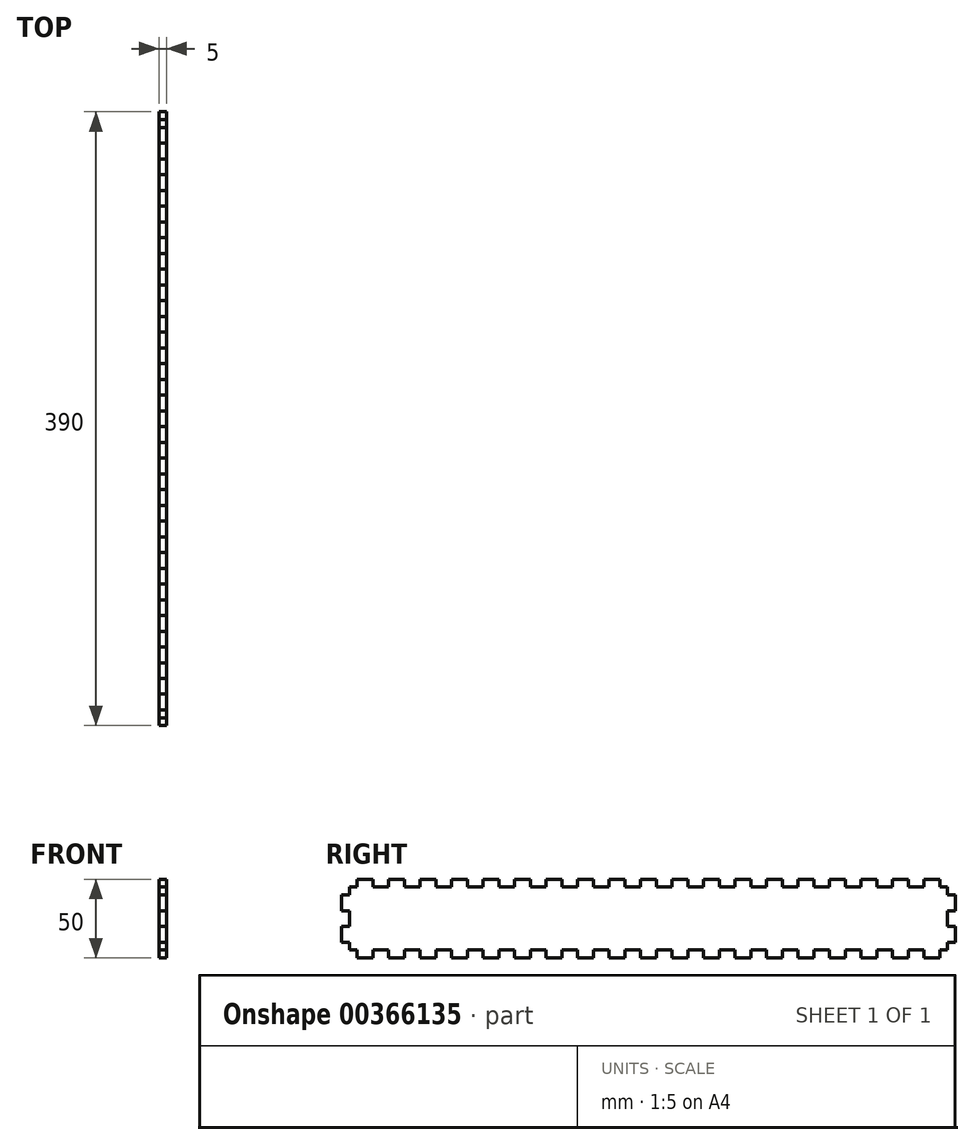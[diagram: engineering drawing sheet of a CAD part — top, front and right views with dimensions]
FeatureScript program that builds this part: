
annotation { "Feature Type Name" : "Feature", "Feature Type Description" : "" }
export const myFeature = defineFeature(function(context is Context, id is Id, definition is map)
    precondition{}
    {
        {
            var Q0;
            Q0=qCreatedBy(makeId("Right.planeOp"),FACE);
            var sketch = newSketch(context, id + "F0", { "sketchPlane" : qUnion([Q0])});
            skPoint(sketch, "E0.middle", {"position": v(0, 0) * mm});
            skLineSegment(sketch, "E1", {"start": v(-125, 20) * mm, "end": v(-125, 25) * mm});
            skLineSegment(sketch, "E2.1.0.0", {"start": v(-125, 25) * mm, "end": v(-115, 25) * mm});
            skLineSegment(sketch, "E2.1.0.1", {"start": v(-115, 25) * mm, "end": v(-115, 20) * mm});
            skLineSegment(sketch, "E2.1.0.2", {"start": v(-115, 20) * mm, "end": v(-105, 20) * mm});
            skLineSegment(sketch, "E2.1.0.3", {"start": v(-105, 20) * mm, "end": v(-105, 25) * mm});
            skLineSegment(sketch, "E2.2.0.0", {"start": v(-105, 25) * mm, "end": v(-95, 25) * mm});
            skLineSegment(sketch, "E2.2.0.1", {"start": v(-95, 25) * mm, "end": v(-95, 20) * mm});
            skLineSegment(sketch, "E2.2.0.2", {"start": v(-95, 20) * mm, "end": v(-85, 20) * mm});
            skLineSegment(sketch, "E2.2.0.3", {"start": v(-85, 20) * mm, "end": v(-85, 25) * mm});
            skLineSegment(sketch, "E2.3.0.0", {"start": v(-85, 25) * mm, "end": v(-75, 25) * mm});
            skLineSegment(sketch, "E2.3.0.1", {"start": v(-75, 25) * mm, "end": v(-75, 20) * mm});
            skLineSegment(sketch, "E2.3.0.2", {"start": v(-75, 20) * mm, "end": v(-65, 20) * mm});
            skLineSegment(sketch, "E2.3.0.3", {"start": v(-65, 20) * mm, "end": v(-65, 25) * mm});
            skLineSegment(sketch, "E2.4.0.0", {"start": v(-65, 25) * mm, "end": v(-55, 25) * mm});
            skLineSegment(sketch, "E2.4.0.1", {"start": v(-55, 25) * mm, "end": v(-55, 20) * mm});
            skLineSegment(sketch, "E2.4.0.2", {"start": v(-55, 20) * mm, "end": v(-45, 20) * mm});
            skLineSegment(sketch, "E2.4.0.3", {"start": v(-45, 20) * mm, "end": v(-45, 25) * mm});
            skLineSegment(sketch, "E2.5.0.0", {"start": v(-45, 25) * mm, "end": v(-35, 25) * mm});
            skLineSegment(sketch, "E2.5.0.1", {"start": v(-35, 25) * mm, "end": v(-35, 20) * mm});
            skLineSegment(sketch, "E2.5.0.2", {"start": v(-35, 20) * mm, "end": v(-25, 20) * mm});
            skLineSegment(sketch, "E2.5.0.3", {"start": v(-25, 20) * mm, "end": v(-25, 25) * mm});
            skLineSegment(sketch, "E2.6.0.0", {"start": v(-25, 25) * mm, "end": v(-15, 25) * mm});
            skLineSegment(sketch, "E2.6.0.1", {"start": v(-15, 25) * mm, "end": v(-15, 20) * mm});
            skLineSegment(sketch, "E2.6.0.2", {"start": v(-15, 20) * mm, "end": v(-5, 20) * mm});
            skLineSegment(sketch, "E2.6.0.3", {"start": v(-5, 20) * mm, "end": v(-5, 25) * mm});
            skLineSegment(sketch, "E2.7.0.0", {"start": v(-5, 25) * mm, "end": v(5, 25) * mm});
            skLineSegment(sketch, "E2.7.0.1", {"start": v(5, 25) * mm, "end": v(5, 20) * mm});
            skLineSegment(sketch, "E2.7.0.2", {"start": v(5, 20) * mm, "end": v(15, 20) * mm});
            skLineSegment(sketch, "E2.7.0.3", {"start": v(15, 20) * mm, "end": v(15, 25) * mm});
            skLineSegment(sketch, "E2.8.0.0", {"start": v(15, 25) * mm, "end": v(25, 25) * mm});
            skLineSegment(sketch, "E2.8.0.1", {"start": v(25, 25) * mm, "end": v(25, 20) * mm});
            skLineSegment(sketch, "E2.8.0.2", {"start": v(25, 20) * mm, "end": v(35, 20) * mm});
            skLineSegment(sketch, "E2.8.0.3", {"start": v(35, 20) * mm, "end": v(35, 25) * mm});
            skLineSegment(sketch, "E2.9.0.0", {"start": v(35, 25) * mm, "end": v(45, 25) * mm});
            skLineSegment(sketch, "E2.9.0.1", {"start": v(45, 25) * mm, "end": v(45, 20) * mm});
            skLineSegment(sketch, "E2.9.0.2", {"start": v(45, 20) * mm, "end": v(55, 20) * mm});
            skLineSegment(sketch, "E2.9.0.3", {"start": v(55, 20) * mm, "end": v(55, 25) * mm});
            skLineSegment(sketch, "E2.10.0.0", {"start": v(55, 25) * mm, "end": v(65, 25) * mm});
            skLineSegment(sketch, "E2.10.0.1", {"start": v(65, 25) * mm, "end": v(65, 20) * mm});
            skLineSegment(sketch, "E2.10.0.2", {"start": v(65, 20) * mm, "end": v(75, 20) * mm});
            skLineSegment(sketch, "E2.10.0.3", {"start": v(75, 20) * mm, "end": v(75, 25) * mm});
            skLineSegment(sketch, "E2.11.0.0", {"start": v(75, 25) * mm, "end": v(85, 25) * mm});
            skLineSegment(sketch, "E2.11.0.1", {"start": v(85, 25) * mm, "end": v(85, 20) * mm});
            skLineSegment(sketch, "E2.11.0.2", {"start": v(85, 20) * mm, "end": v(95, 20) * mm});
            skLineSegment(sketch, "E2.11.0.3", {"start": v(95, 20) * mm, "end": v(95, 25) * mm});
            skLineSegment(sketch, "E2.12.0.0", {"start": v(95, 25) * mm, "end": v(105, 25) * mm});
            skLineSegment(sketch, "E2.12.0.1", {"start": v(105, 25) * mm, "end": v(105, 20) * mm});
            skLineSegment(sketch, "E2.12.0.2", {"start": v(105, 20) * mm, "end": v(115, 20) * mm});
            skLineSegment(sketch, "E2.12.0.3", {"start": v(115, 20) * mm, "end": v(115, 25) * mm});
            skLineSegment(sketch, "E2.13.0.0", {"start": v(115, 25) * mm, "end": v(125, 25) * mm});
            skLineSegment(sketch, "E2.13.0.1", {"start": v(125, 25) * mm, "end": v(125, 20) * mm});
            skLineSegment(sketch, "E2.13.0.2", {"start": v(125, 20) * mm, "end": v(135, 20) * mm});
            skLineSegment(sketch, "E2.13.0.3", {"start": v(135, 20) * mm, "end": v(135, 25) * mm});
            skLineSegment(sketch, "E3", {"start": v(135, 25) * mm, "end": v(145, 25) * mm});
            skLineSegment(sketch, "E4", {"start": v(-125, -20) * mm, "end": v(-125, -25) * mm});
            skLineSegment(sketch, "E5.1.0.0", {"start": v(-125, -25) * mm, "end": v(-115, -25) * mm});
            skLineSegment(sketch, "E5.1.0.1", {"start": v(-115, -25) * mm, "end": v(-115, -20) * mm});
            skLineSegment(sketch, "E5.1.0.2", {"start": v(-115, -20) * mm, "end": v(-105, -20) * mm});
            skLineSegment(sketch, "E5.1.0.3", {"start": v(-105, -20) * mm, "end": v(-105, -25) * mm});
            skLineSegment(sketch, "E5.2.0.0", {"start": v(-105, -25) * mm, "end": v(-95, -25) * mm});
            skLineSegment(sketch, "E5.2.0.1", {"start": v(-95, -25) * mm, "end": v(-95, -20) * mm});
            skLineSegment(sketch, "E5.2.0.2", {"start": v(-95, -20) * mm, "end": v(-85, -20) * mm});
            skLineSegment(sketch, "E5.2.0.3", {"start": v(-85, -20) * mm, "end": v(-85, -25) * mm});
            skLineSegment(sketch, "E5.3.0.0", {"start": v(-85, -25) * mm, "end": v(-75, -25) * mm});
            skLineSegment(sketch, "E5.3.0.1", {"start": v(-75, -25) * mm, "end": v(-75, -20) * mm});
            skLineSegment(sketch, "E5.3.0.2", {"start": v(-75, -20) * mm, "end": v(-65, -20) * mm});
            skLineSegment(sketch, "E5.3.0.3", {"start": v(-65, -20) * mm, "end": v(-65, -25) * mm});
            skLineSegment(sketch, "E5.4.0.0", {"start": v(-65, -25) * mm, "end": v(-55, -25) * mm});
            skLineSegment(sketch, "E5.4.0.1", {"start": v(-55, -25) * mm, "end": v(-55, -20) * mm});
            skLineSegment(sketch, "E5.4.0.2", {"start": v(-55, -20) * mm, "end": v(-45, -20) * mm});
            skLineSegment(sketch, "E5.4.0.3", {"start": v(-45, -20) * mm, "end": v(-45, -25) * mm});
            skLineSegment(sketch, "E5.5.0.0", {"start": v(-45, -25) * mm, "end": v(-35, -25) * mm});
            skLineSegment(sketch, "E5.5.0.1", {"start": v(-35, -25) * mm, "end": v(-35, -20) * mm});
            skLineSegment(sketch, "E5.5.0.2", {"start": v(-35, -20) * mm, "end": v(-25, -20) * mm});
            skLineSegment(sketch, "E5.5.0.3", {"start": v(-25, -20) * mm, "end": v(-25, -25) * mm});
            skLineSegment(sketch, "E5.6.0.0", {"start": v(-25, -25) * mm, "end": v(-15, -25) * mm});
            skLineSegment(sketch, "E5.6.0.1", {"start": v(-15, -25) * mm, "end": v(-15, -20) * mm});
            skLineSegment(sketch, "E5.6.0.2", {"start": v(-15, -20) * mm, "end": v(-5, -20) * mm});
            skLineSegment(sketch, "E5.6.0.3", {"start": v(-5, -20) * mm, "end": v(-5, -25) * mm});
            skLineSegment(sketch, "E5.7.0.0", {"start": v(-5, -25) * mm, "end": v(5, -25) * mm});
            skLineSegment(sketch, "E5.7.0.1", {"start": v(5, -25) * mm, "end": v(5, -20) * mm});
            skLineSegment(sketch, "E5.7.0.2", {"start": v(5, -20) * mm, "end": v(15, -20) * mm});
            skLineSegment(sketch, "E5.7.0.3", {"start": v(15, -20) * mm, "end": v(15, -25) * mm});
            skLineSegment(sketch, "E5.8.0.0", {"start": v(15, -25) * mm, "end": v(25, -25) * mm});
            skLineSegment(sketch, "E5.8.0.1", {"start": v(25, -25) * mm, "end": v(25, -20) * mm});
            skLineSegment(sketch, "E5.8.0.2", {"start": v(25, -20) * mm, "end": v(35, -20) * mm});
            skLineSegment(sketch, "E5.8.0.3", {"start": v(35, -20) * mm, "end": v(35, -25) * mm});
            skLineSegment(sketch, "E5.9.0.0", {"start": v(35, -25) * mm, "end": v(45, -25) * mm});
            skLineSegment(sketch, "E5.9.0.1", {"start": v(45, -25) * mm, "end": v(45, -20) * mm});
            skLineSegment(sketch, "E5.9.0.2", {"start": v(45, -20) * mm, "end": v(55, -20) * mm});
            skLineSegment(sketch, "E5.9.0.3", {"start": v(55, -20) * mm, "end": v(55, -25) * mm});
            skLineSegment(sketch, "E5.10.0.0", {"start": v(55, -25) * mm, "end": v(65, -25) * mm});
            skLineSegment(sketch, "E5.10.0.1", {"start": v(65, -25) * mm, "end": v(65, -20) * mm});
            skLineSegment(sketch, "E5.10.0.2", {"start": v(65, -20) * mm, "end": v(75, -20) * mm});
            skLineSegment(sketch, "E5.10.0.3", {"start": v(75, -20) * mm, "end": v(75, -25) * mm});
            skLineSegment(sketch, "E5.11.0.0", {"start": v(75, -25) * mm, "end": v(85, -25) * mm});
            skLineSegment(sketch, "E5.11.0.1", {"start": v(85, -25) * mm, "end": v(85, -20) * mm});
            skLineSegment(sketch, "E5.11.0.2", {"start": v(85, -20) * mm, "end": v(95, -20) * mm});
            skLineSegment(sketch, "E5.11.0.3", {"start": v(95, -20) * mm, "end": v(95, -25) * mm});
            skLineSegment(sketch, "E5.12.0.0", {"start": v(95, -25) * mm, "end": v(105, -25) * mm});
            skLineSegment(sketch, "E5.12.0.1", {"start": v(105, -25) * mm, "end": v(105, -20) * mm});
            skLineSegment(sketch, "E5.12.0.2", {"start": v(105, -20) * mm, "end": v(115, -20) * mm});
            skLineSegment(sketch, "E5.12.0.3", {"start": v(115, -20) * mm, "end": v(115, -25) * mm});
            skLineSegment(sketch, "E5.13.0.0", {"start": v(115, -25) * mm, "end": v(125, -25) * mm});
            skLineSegment(sketch, "E5.13.0.1", {"start": v(125, -25) * mm, "end": v(125, -20) * mm});
            skLineSegment(sketch, "E5.13.0.2", {"start": v(125, -20) * mm, "end": v(135, -20) * mm});
            skLineSegment(sketch, "E5.13.0.3", {"start": v(135, -20) * mm, "end": v(135, -25) * mm});
            skLineSegment(sketch, "E6", {"start": v(135, -25) * mm, "end": v(145, -25) * mm});
            skLineSegment(sketch, "E7", {"start": v(-130, 20) * mm, "end": v(-125, 20) * mm});
            skLineSegment(sketch, "E8", {"start": v(-130, -20) * mm, "end": v(-125, -20) * mm});
            skLineSegment(sketch, "E9", {"start": v(-130, 20) * mm, "end": v(-130, 15) * mm});
            skLineSegment(sketch, "E10", {"start": v(-130, 15) * mm, "end": v(-135, 15) * mm});
            skLineSegment(sketch, "E11", {"start": v(-135, 15) * mm, "end": v(-135, 5) * mm});
            skLineSegment(sketch, "E12", {"start": v(-135, 5) * mm, "end": v(-130, 5) * mm});
            skLineSegment(sketch, "E13", {"start": v(-130, 5) * mm, "end": v(-130, -5) * mm});
            skLineSegment(sketch, "E14", {"start": v(-130, -5) * mm, "end": v(-135, -5) * mm});
            skLineSegment(sketch, "E15", {"start": v(-135, -5) * mm, "end": v(-135, -15) * mm});
            skLineSegment(sketch, "E16", {"start": v(-135, -15) * mm, "end": v(-130, -15) * mm});
            skLineSegment(sketch, "E17", {"start": v(-130, -15) * mm, "end": v(-130, -20) * mm});
            skLineSegment(sketch, "E18", {"start": v(145, 25) * mm, "end": v(145, 20) * mm});
            skLineSegment(sketch, "E19", {"start": v(145, -25) * mm, "end": v(145, -20) * mm});
            skLineSegment(sketch, "E20", {"start": v(245, 20) * mm, "end": v(250, 20) * mm});
            skLineSegment(sketch, "E21", {"start": v(245, -20) * mm, "end": v(250, -20) * mm});
            skLineSegment(sketch, "E22", {"start": v(250, -20) * mm, "end": v(250, -15) * mm});
            skLineSegment(sketch, "E23", {"start": v(250, -15) * mm, "end": v(255, -15) * mm});
            skLineSegment(sketch, "E24", {"start": v(255, -15) * mm, "end": v(255, -5) * mm});
            skLineSegment(sketch, "E25", {"start": v(255, -5) * mm, "end": v(250, -5) * mm});
            skLineSegment(sketch, "E26", {"start": v(250, -5) * mm, "end": v(250, 5) * mm});
            skLineSegment(sketch, "E27", {"start": v(250, 5) * mm, "end": v(255, 5) * mm});
            skLineSegment(sketch, "E28", {"start": v(255, 5) * mm, "end": v(255, 15) * mm});
            skLineSegment(sketch, "E29", {"start": v(255, 15) * mm, "end": v(250, 15) * mm});
            skLineSegment(sketch, "E30", {"start": v(250, 15) * mm, "end": v(250, 20) * mm});
            skLineSegment(sketch, "E31.9.0.2", {"start": v(145, 20) * mm, "end": v(155, 20) * mm});
            skLineSegment(sketch, "E31.9.0.3", {"start": v(155, 20) * mm, "end": v(155, 25) * mm});
            skLineSegment(sketch, "E31.10.0.0", {"start": v(155, 25) * mm, "end": v(165, 25) * mm});
            skLineSegment(sketch, "E31.10.0.1", {"start": v(165, 25) * mm, "end": v(165, 20) * mm});
            skLineSegment(sketch, "E31.10.0.2", {"start": v(165, 20) * mm, "end": v(175, 20) * mm});
            skLineSegment(sketch, "E31.10.0.3", {"start": v(175, 20) * mm, "end": v(175, 25) * mm});
            skLineSegment(sketch, "E31.11.0.0", {"start": v(175, 25) * mm, "end": v(185, 25) * mm});
            skLineSegment(sketch, "E31.11.0.1", {"start": v(185, 25) * mm, "end": v(185, 20) * mm});
            skLineSegment(sketch, "E31.11.0.2", {"start": v(185, 20) * mm, "end": v(195, 20) * mm});
            skLineSegment(sketch, "E31.11.0.3", {"start": v(195, 20) * mm, "end": v(195, 25) * mm});
            skLineSegment(sketch, "E31.12.0.0", {"start": v(195, 25) * mm, "end": v(205, 25) * mm});
            skLineSegment(sketch, "E31.12.0.1", {"start": v(205, 25) * mm, "end": v(205, 20) * mm});
            skLineSegment(sketch, "E31.12.0.2", {"start": v(205, 20) * mm, "end": v(215, 20) * mm});
            skLineSegment(sketch, "E31.12.0.3", {"start": v(215, 20) * mm, "end": v(215, 25) * mm});
            skLineSegment(sketch, "E31.13.0.0", {"start": v(215, 25) * mm, "end": v(225, 25) * mm});
            skLineSegment(sketch, "E31.13.0.1", {"start": v(225, 25) * mm, "end": v(225, 20) * mm});
            skLineSegment(sketch, "E31.13.0.2", {"start": v(225, 20) * mm, "end": v(235, 20) * mm});
            skLineSegment(sketch, "E31.13.0.3", {"start": v(235, 20) * mm, "end": v(235, 25) * mm});
            skLineSegment(sketch, "E32", {"start": v(235, 25) * mm, "end": v(245, 25) * mm});
            skLineSegment(sketch, "E33", {"start": v(245, 25) * mm, "end": v(245, 20) * mm});
            skLineSegment(sketch, "E34.9.0.2", {"start": v(145, -20) * mm, "end": v(155, -20) * mm});
            skLineSegment(sketch, "E34.9.0.3", {"start": v(155, -20) * mm, "end": v(155, -25) * mm});
            skLineSegment(sketch, "E34.10.0.0", {"start": v(155, -25) * mm, "end": v(165, -25) * mm});
            skLineSegment(sketch, "E34.10.0.1", {"start": v(165, -25) * mm, "end": v(165, -20) * mm});
            skLineSegment(sketch, "E34.10.0.2", {"start": v(165, -20) * mm, "end": v(175, -20) * mm});
            skLineSegment(sketch, "E34.10.0.3", {"start": v(175, -20) * mm, "end": v(175, -25) * mm});
            skLineSegment(sketch, "E34.11.0.0", {"start": v(175, -25) * mm, "end": v(185, -25) * mm});
            skLineSegment(sketch, "E34.11.0.1", {"start": v(185, -25) * mm, "end": v(185, -20) * mm});
            skLineSegment(sketch, "E34.11.0.2", {"start": v(185, -20) * mm, "end": v(195, -20) * mm});
            skLineSegment(sketch, "E34.11.0.3", {"start": v(195, -20) * mm, "end": v(195, -25) * mm});
            skLineSegment(sketch, "E34.12.0.0", {"start": v(195, -25) * mm, "end": v(205, -25) * mm});
            skLineSegment(sketch, "E34.12.0.1", {"start": v(205, -25) * mm, "end": v(205, -20) * mm});
            skLineSegment(sketch, "E34.12.0.2", {"start": v(205, -20) * mm, "end": v(215, -20) * mm});
            skLineSegment(sketch, "E34.12.0.3", {"start": v(215, -20) * mm, "end": v(215, -25) * mm});
            skLineSegment(sketch, "E34.13.0.0", {"start": v(215, -25) * mm, "end": v(225, -25) * mm});
            skLineSegment(sketch, "E34.13.0.1", {"start": v(225, -25) * mm, "end": v(225, -20) * mm});
            skLineSegment(sketch, "E34.13.0.2", {"start": v(225, -20) * mm, "end": v(235, -20) * mm});
            skLineSegment(sketch, "E34.13.0.3", {"start": v(235, -20) * mm, "end": v(235, -25) * mm});
            skLineSegment(sketch, "E35", {"start": v(235, -25) * mm, "end": v(245, -25) * mm});
            skLineSegment(sketch, "E36", {"start": v(245, -25) * mm, "end": v(245, -20) * mm});
            skSolve(sketch);
        }
        {
            var Q0;
            Q0=qSketchRegion(id+"F0",true);
            extrude(context, id + "F1", {"entities" : qUnion([Q0]), "endBound" : BoundingType.SYMMETRIC, "depth" : 5 * mm});
        }
    });
